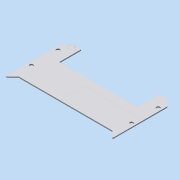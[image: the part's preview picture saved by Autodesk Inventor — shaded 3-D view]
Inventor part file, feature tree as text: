
AUTODESK INVENTOR PART (.ipt)
format: ipt  version: 2015 (Build 190159000, 159)  size: 441,856 bytes
history: native  units: in
note: dims shown in document units (in); Inventor stores cm internally (conversion verified against a paired STEP export)
features: other x4, extrude x1, fillet x1, sketch x1, projected_geometry x1
ambient origin geometry x8: Origin, YZ Plane, XZ Plane, XY Plane, X Axis, Y Axis, Z Axis, Center Point
bodies: Solid1 (feature_tree)
feature tree (8):
  other  "BatteryEnclosure.ipt"
  extrude  "Extrusion1"  Depth=0.0625in TaperAngle=0.0deg
  fillet  "Fillet1"  Radius=0.0312in
  other  "TaggingFeature1"
  sketch  "Sketch1"  dims[d0=0.3937in d2=0.0625in d3=0.0in d4=0.0312in d5=0.0312in d6=0.0312in d8=1.25in]
  other  "Solid2::BatteryEnclosure.ipt"
  other  "Srf1"
  projected_geometry  "Project Cut Edges1"
